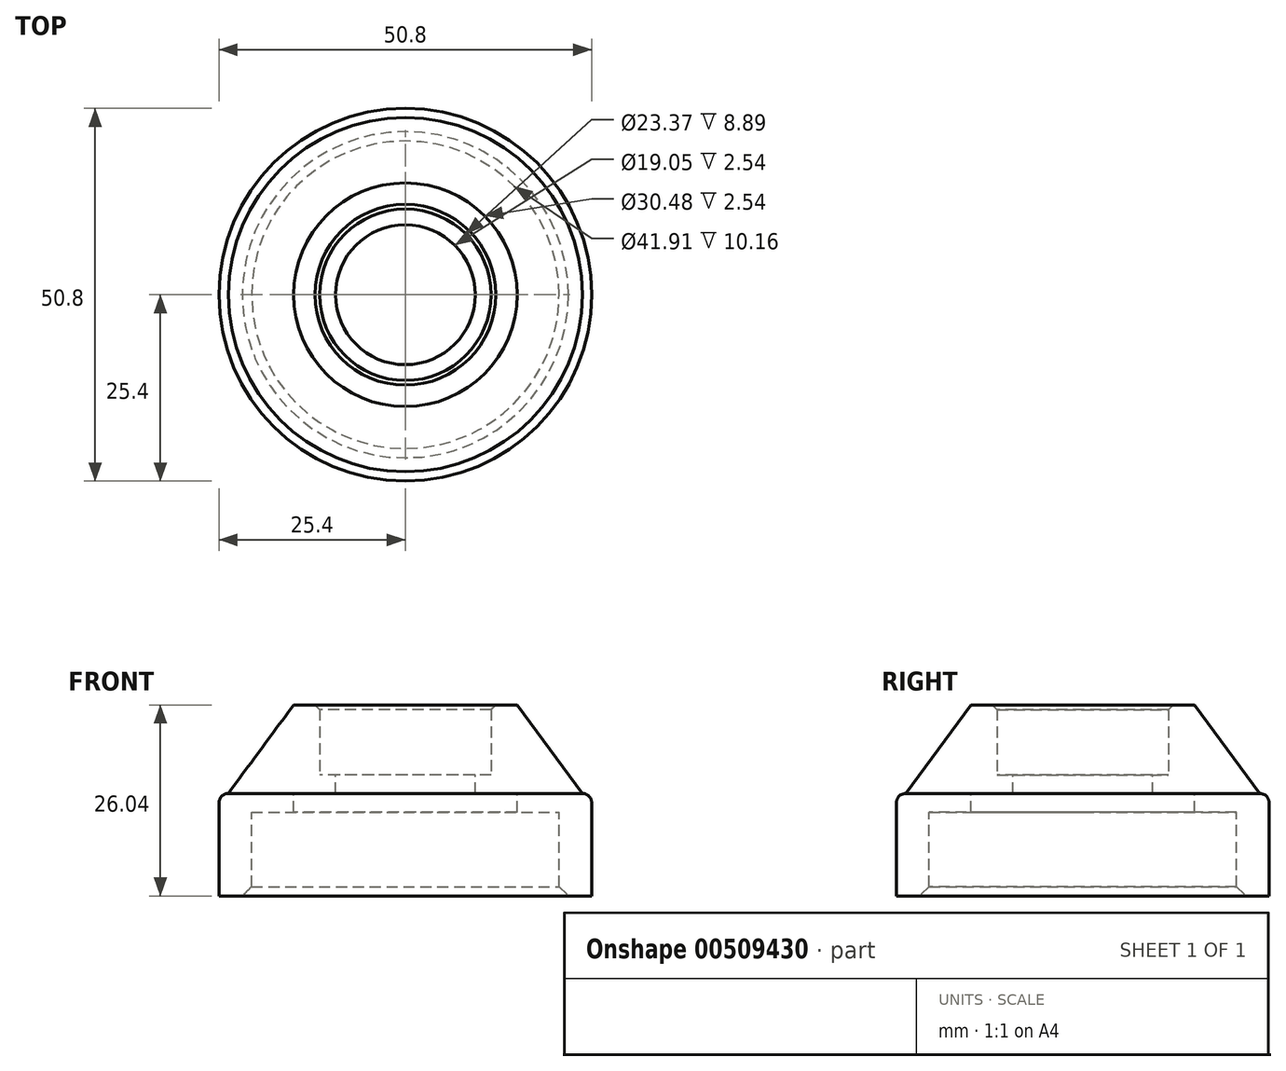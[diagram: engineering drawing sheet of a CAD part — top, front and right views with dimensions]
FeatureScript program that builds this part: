
annotation { "Feature Type Name" : "Feature", "Feature Type Description" : "" }
export const myFeature = defineFeature(function(context is Context, id is Id, definition is map)
    precondition{}
    {
        {
            var Q0;
            Q0=qCreatedBy(makeId("Top.planeOp"),FACE);
            var sketch = newSketch(context, id + "F0", { "sketchPlane" : qUnion([Q0])});
            skArc(sketch, "E0", {"start": v(10.74, 10.8) * mm, "mid": v(-15.24, 0) * mm, "end": v(10.74, -10.8) * mm});
            skArc(sketch, "E1", {"start": v(25.4, -4.76) * mm, "mid": v(30.16, 0) * mm, "end": v(25.4, 4.76) * mm});
            skLineSegment(sketch, "E2", {"start": v(10.74, -10.8) * mm, "end": v(25.4, -4.76) * mm});
            skPoint(sketch, "E3.orphan", {"position": v(25.4, 4.76) * mm});
            skPoint(sketch, "E4.start.orphan", {"position": v(0, 15.24) * mm});
            skLineSegment(sketch, "E5", {"start": v(10.74, 10.8) * mm, "end": v(25.4, 4.76) * mm});
            skPoint(sketch, "E6.orphan", {"position": v(0, -15.24) * mm});
            skSolve(sketch);
        }
        {
            var Q0;
            Q0=makeQuery(id+"F0.imprint","IMPRINT",FACE,{"disambiguationData":[TD([[makeQuery(id+"F0.imprint","IMPRINT",EDGE,{"derivedFrom":sQuery(id+"F0.wireOp",EDGE,"E0")}),1.0]])]});
            extrude(context, id + "F1", {"entities" : qUnion([Q0]), "depth" : 2.54 * mm});
        }
        {
            var Q0;
            Q0=makeQuery(id+"F1.opExtrude","CAP_FACE",FACE,{"disambiguationData":[OSD([sQuery(id+"F0.wireOp",EDGE,"E0"),sQuery(id+"F0.wireOp",EDGE,"E1"),sQuery(id+"F0.wireOp",EDGE,"E2"),sQuery(id+"F0.wireOp",EDGE,"E5")])],"isStart":false});
            var sketch = newSketch(context, id + "F2", { "sketchPlane" : qUnion([Q0])});
            skCircle(sketch, "E7", {"center": v(0, 0) * mm, "radius": 15.24 * mm});
            skCircle(sketch, "E8", {"center": v(0, 0) * mm, "radius": 11.68 * mm});
            skSolve(sketch);
        }
        {
            var Q0;
            Q0=makeQuery(id+"F2.imprint","IMPRINT",FACE,{"disambiguationData":[TD([[makeQuery(id+"F2.imprint","IMPRINT",EDGE,{"derivedFrom":sQuery(id+"F2.wireOp",EDGE,"E8")}),-1.0]])]});
            extrude(context, id + "F3", {"entities" : qUnion([Q0]), "operationType" : NewBodyOperationType.ADD, "depth" : 9.52 * mm});
        }
        {
            var Q0;
            Q0=makeQuery(id+"F3.opExtrude","CAP_EDGE",EDGE,{"disambiguationData":[OSD([sQuery(id+"F2.wireOp",EDGE,"E8")])],"isStart":false});
            chamfer(context, id + "F4", {"entities" : qUnion([Q0]), "width" : 0.64 * mm, "tangentPropagation" : true});
        }
        {
            var Q0;
            Q0=makeQuery(id+"F1.opExtrude","CAP_FACE",FACE,{"disambiguationData":[OSD([sQuery(id+"F0.wireOp",EDGE,"E0"),sQuery(id+"F0.wireOp",EDGE,"E1"),sQuery(id+"F0.wireOp",EDGE,"E2"),sQuery(id+"F0.wireOp",EDGE,"E5")])],"isStart":true});
            var sketch = newSketch(context, id + "F5", { "sketchPlane" : qUnion([Q0])});
            skCircle(sketch, "E9", {"center": v(0, 0) * mm, "radius": 15.24 * mm});
            skSolve(sketch);
        }
        {
            var Q0;
            Q0=makeQuery(id+"F5.imprint","IMPRINT",FACE,{"disambiguationData":[TD([[makeQuery(id+"F5.imprint","IMPRINT",EDGE,{"disambiguationData":[OD(1.0)],"derivedFrom":sQuery(id+"F5.wireOp",EDGE,"E9")}),-1.0]])]});
            extrude(context, id + "F6", {"entities" : qUnion([Q0]), "operationType" : NewBodyOperationType.REMOVE, "endBound" : BoundingType.THROUGH_ALL, "oppositeDirection" : true, "depth" : 25.4 * mm});
        }
        {
            var Q0;
            Q0=makeQuery(id+"F1.opExtrude","CAP_FACE",FACE,{"disambiguationData":[OSD([sQuery(id+"F0.wireOp",EDGE,"E0"),sQuery(id+"F0.wireOp",EDGE,"E1"),sQuery(id+"F0.wireOp",EDGE,"E2"),sQuery(id+"F0.wireOp",EDGE,"E5")])],"isStart":true});
            var sketch = newSketch(context, id + "F7", { "sketchPlane" : qUnion([Q0])});
            skCircle(sketch, "E10", {"center": v(0, 0) * mm, "radius": 25.4 * mm});
            skSolve(sketch);
        }
        {
            var Q0;
            Q0=makeQuery(id+"F7.imprint","IMPRINT",FACE,{"disambiguationData":[TD([[makeQuery(id+"F7.imprint","IMPRINT",EDGE,{"derivedFrom":sQuery(id+"F7.wireOp",EDGE,"E10")}),1.0]])]});
            var Q1;
            Q1=makeQuery(id+"F7.imprint","IMPRINT",FACE,{"disambiguationData":[TD([[makeQuery(id+"F7.imprint","IMPRINT",EDGE,{"derivedFrom":makeQuery(id+"F6.boolean.opBoolean","MERGE",EDGE,{"derivedFrom":[makeQuery(id+"F1.opExtrude","CAP_EDGE",EDGE,{"disambiguationData":[OSD([sQuery(id+"F0.wireOp",EDGE,"E0")])],"isStart":true}),makeQuery(id+"F6.opExtrude","CAP_EDGE",EDGE,{"disambiguationData":[OSD([sQuery(id+"F5.wireOp",EDGE,"E9")])],"isStart":true})]})}),-1.0]])]});
            extrude(context, id + "F8", {"entities" : qUnion([Q0, Q1]), "operationType" : NewBodyOperationType.ADD, "depth" : 2.54 * mm});
        }
        {
            var Q0;
            Q0=makeQuery(id+"F8.opExtrude","CAP_FACE",FACE,{"disambiguationData":[OSD([sQuery(id+"F7.wireOp",EDGE,"E10")])],"isStart":false});
            var sketch = newSketch(context, id + "F9", { "sketchPlane" : qUnion([Q0])});
            skCircle(sketch, "E11", {"center": v(0, 0) * mm, "radius": 25.4 * mm});
            skCircle(sketch, "E12", {"center": v(0, 0) * mm, "radius": 20.96 * mm});
            skSolve(sketch);
        }
        {
            var Q0;
            Q0=makeQuery(id+"F9.imprint","IMPRINT",FACE,{"disambiguationData":[TD([[makeQuery(id+"F9.imprint","IMPRINT",EDGE,{"derivedFrom":sQuery(id+"F9.wireOp",EDGE,"E11")}),1.0]])]});
            extrude(context, id + "F10", {"entities" : qUnion([Q0]), "operationType" : NewBodyOperationType.ADD, "depth" : 11.43 * mm, "offsetDistance" : 25.4 * mm});
        }
        {
            var Q0;
            Q0=makeQuery(id+"F10.opExtrude","CAP_EDGE",EDGE,{"disambiguationData":[OSD([sQuery(id+"F9.wireOp",EDGE,"E12")])],"isStart":false});
            chamfer(context, id + "F11", {"entities" : qUnion([Q0]), "width" : 1.27 * mm, "tangentPropagation" : true});
        }
        {
            var Q0;
            Q0=makeQuery(id+"F3.boolean.opBoolean","SPLIT",FACE,{"disambiguationData":[TD([makeQuery(id+"F3.opExtrude","SWEPT_FACE",FACE,{"disambiguationData":[OSD([sQuery(id+"F2.wireOp",EDGE,"E8")])]})])],"derivedFrom":makeQuery(id+"F1.opExtrude","CAP_FACE",FACE,{"disambiguationData":[OSD([sQuery(id+"F0.wireOp",EDGE,"E0"),sQuery(id+"F0.wireOp",EDGE,"E1"),sQuery(id+"F0.wireOp",EDGE,"E2"),sQuery(id+"F0.wireOp",EDGE,"E5")])],"isStart":false})});
            var sketch = newSketch(context, id + "F12", { "sketchPlane" : qUnion([Q0])});
            skCircle(sketch, "E13", {"center": v(0, 0) * mm, "radius": 9.53 * mm});
            skSolve(sketch);
        }
        {
            var Q0;
            Q0=makeQuery(id+"F12.imprint","IMPRINT",FACE,{"disambiguationData":[TD([[makeQuery(id+"F12.imprint","IMPRINT",EDGE,{"derivedFrom":sQuery(id+"F12.wireOp",EDGE,"E13")}),1.0]])]});
            extrude(context, id + "F13", {"entities" : qUnion([Q0]), "operationType" : NewBodyOperationType.REMOVE, "endBound" : BoundingType.THROUGH_ALL, "oppositeDirection" : true, "depth" : 25.4 * mm});
        }
        {
            var Q0;
            Q0=makeQuery(id+"F8.opExtrude","CAP_EDGE",EDGE,{"disambiguationData":[OSD([sQuery(id+"F7.wireOp",EDGE,"E10")])],"isStart":true});
            fillet(context, id + "F14", {"entities" : qUnion([Q0]), "radius" : 1.27 * mm, "tangentPropagation" : true, "allowEdgeOverflow" : false});
        }
        {
            var Q0;
            Q0=qCreatedBy(makeId("Front.planeOp"),FACE);
            var sketch = newSketch(context, id + "F15", { "sketchPlane" : qUnion([Q0])});
            skLineSegment(sketch, "E14", {"start": v(15.24, 0) * mm, "end": v(15.24, 12.07) * mm});
            skLineSegment(sketch, "E15", {"start": v(15.24, 12.07) * mm, "end": v(24.13, 0) * mm});
            skLineSegment(sketch, "E16", {"start": v(24.13, 0) * mm, "end": v(15.24, 0) * mm});
            skSolve(sketch);
        }
        {
            var Q0;
            Q0=makeQuery(id+"F15.imprint","IMPRINT",FACE,{"disambiguationData":[TD([[makeQuery(id+"F15.imprint","IMPRINT",EDGE,{"derivedFrom":sQuery(id+"F15.wireOp",EDGE,"E14")}),-1.0]])]});
            var Q1;
            Q1=makeQuery(id+"F3.opExtrude","SWEPT_FACE",FACE,{"disambiguationData":[OSD([sQuery(id+"F2.wireOp",EDGE,"E8")])]});
            revolve(context, id + "F16", {"operationType" : NewBodyOperationType.ADD, "entities" : qUnion([Q0]), "axis" : qUnion([Q1]), "revolveType" : RevolveType.FULL});
        }
    });
